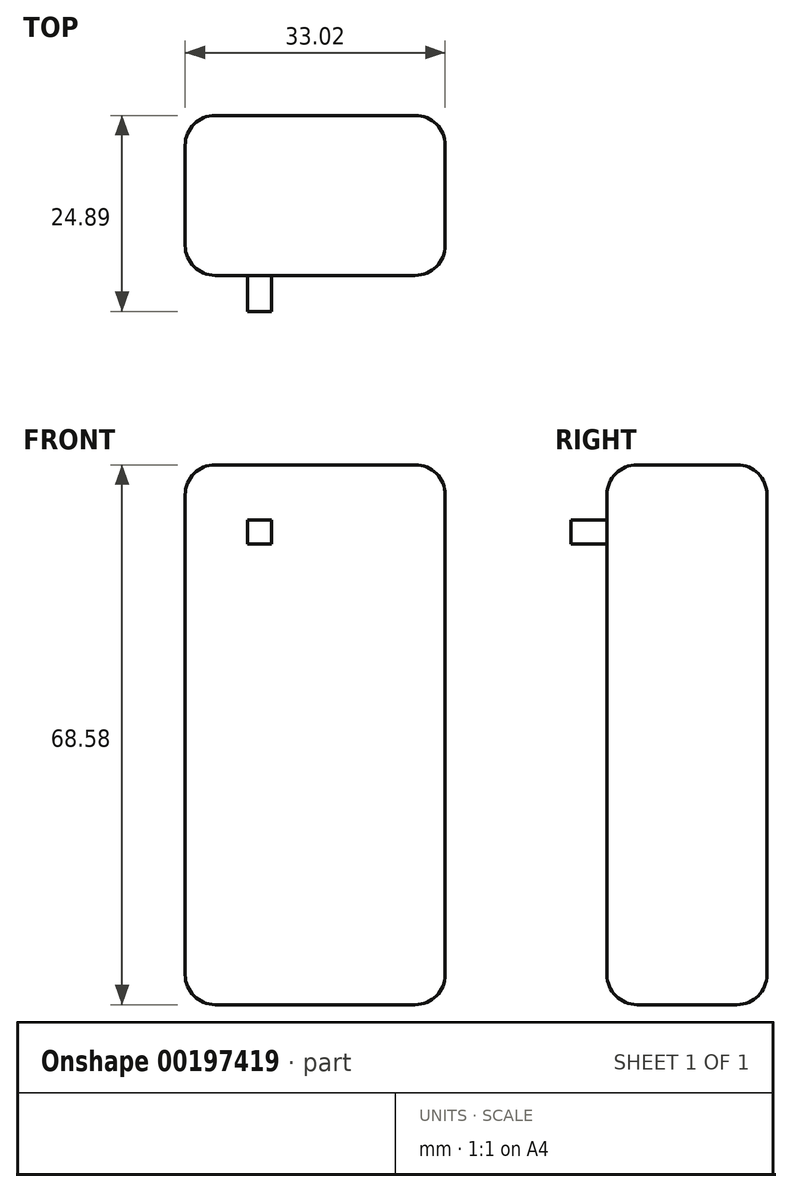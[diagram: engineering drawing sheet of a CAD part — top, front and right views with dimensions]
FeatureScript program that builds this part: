
annotation { "Feature Type Name" : "Feature", "Feature Type Description" : "" }
export const myFeature = defineFeature(function(context is Context, id is Id, definition is map)
    precondition{}
    {
        {
            var Q0;
            Q0=qCreatedBy(makeId("Front.planeOp"),FACE);
            var sketch = newSketch(context, id + "F0", { "sketchPlane" : qUnion([Q0])});
            skLineSegment(sketch, "E0.bottom", {"start": v(0, 0) * mm, "end": v(33.02, 0) * mm});
            skLineSegment(sketch, "E0.top", {"start": v(0, 68.58) * mm, "end": v(33.02, 68.58) * mm});
            skLineSegment(sketch, "E0.left", {"start": v(0, 0) * mm, "end": v(0, 68.58) * mm});
            skLineSegment(sketch, "E0.right", {"start": v(33.02, 0) * mm, "end": v(33.02, 68.58) * mm});
            skSolve(sketch);
        }
        {
            var Q0;
            Q0 = qSketchRegion(id + "F0", true);
            extrude(context, id + "F1", {"entities" : qUnion([Q0]), "depth" : 20.32 * mm});
        }
        {
            var Q0;
            Q0=makeQuery(id+"F1.opExtrude","CAP_EDGE",EDGE,{"disambiguationData":[OSD([sQuery(id+"F0.wireOp",EDGE,"E0.right")])],"isStart":false});
            var Q1;
            Q1=makeQuery(id+"F1.opExtrude","SWEPT_EDGE",EDGE,{"disambiguationData":[OSD([sQuery(id+"F0.wireOp",EDGE,"E0.top"),sQuery(id+"F0.wireOp",EDGE,"E0.right")])]});
            var Q2;
            Q2=makeQuery(id+"F1.opExtrude","CAP_EDGE",EDGE,{"disambiguationData":[OSD([sQuery(id+"F0.wireOp",EDGE,"E0.top")])],"isStart":false});
            var Q3;
            Q3=makeQuery(id+"F1.opExtrude","CAP_EDGE",EDGE,{"disambiguationData":[OSD([sQuery(id+"F0.wireOp",EDGE,"E0.left")])],"isStart":false});
            var Q4;
            Q4=makeQuery(id+"F1.opExtrude","CAP_EDGE",EDGE,{"disambiguationData":[OSD([sQuery(id+"F0.wireOp",EDGE,"E0.bottom")])],"isStart":false});
            var Q5;
            Q5=makeQuery(id+"F1.opExtrude","SWEPT_EDGE",EDGE,{"disambiguationData":[OSD([sQuery(id+"F0.wireOp",EDGE,"E0.bottom"),sQuery(id+"F0.wireOp",EDGE,"E0.right")])]});
            var Q6;
            Q6=makeQuery(id+"F1.opExtrude","CAP_EDGE",EDGE,{"disambiguationData":[OSD([sQuery(id+"F0.wireOp",EDGE,"E0.right")])],"isStart":true});
            var Q7;
            Q7=makeQuery(id+"F1.opExtrude","CAP_EDGE",EDGE,{"disambiguationData":[OSD([sQuery(id+"F0.wireOp",EDGE,"E0.bottom")])],"isStart":true});
            var Q8;
            Q8=makeQuery(id+"F1.opExtrude","CAP_EDGE",EDGE,{"disambiguationData":[OSD([sQuery(id+"F0.wireOp",EDGE,"E0.left")])],"isStart":true});
            var Q9;
            Q9=makeQuery(id+"F1.opExtrude","SWEPT_FACE",FACE,{"disambiguationData":[OSD([sQuery(id+"F0.wireOp",EDGE,"E0.left")])]});
            var Q10;
            Q10=makeQuery(id+"F1.opExtrude","SWEPT_FACE",FACE,{"disambiguationData":[OSD([sQuery(id+"F0.wireOp",EDGE,"E0.top")])]});
            fillet(context, id + "F2", {"entities" : qUnion([Q0, Q1, Q2, Q3, Q4, Q5, Q6, Q7, Q8, Q9, Q10]), "radius" : 3.8 * mm, "tangentPropagation" : true, "allowEdgeOverflow" : false});
        }
        {
            var Q0;
            Q0=makeQuery(id+"F1.opExtrude","CAP_FACE",FACE,{"disambiguationData":[OSD([sQuery(id+"F0.wireOp",EDGE,"E0.bottom"),sQuery(id+"F0.wireOp",EDGE,"E0.top"),sQuery(id+"F0.wireOp",EDGE,"E0.left"),sQuery(id+"F0.wireOp",EDGE,"E0.right")])],"isStart":false});
            var sketch = newSketch(context, id + "F3", { "sketchPlane" : qUnion([Q0])});
            skLineSegment(sketch, "E1.bottom", {"start": v(7.9, 61.57) * mm, "end": v(10.98, 61.57) * mm});
            skLineSegment(sketch, "E1.top", {"start": v(7.9, 58.5) * mm, "end": v(10.98, 58.5) * mm});
            skLineSegment(sketch, "E1.left", {"start": v(7.9, 61.57) * mm, "end": v(7.9, 58.5) * mm});
            skLineSegment(sketch, "E1.right", {"start": v(10.98, 61.57) * mm, "end": v(10.98, 58.5) * mm});
            skSolve(sketch);
        }
        {
            var Q0;
            Q0 = qSketchRegion(id + "F3", true);
            extrude(context, id + "F4", {"entities" : qUnion([Q0]), "operationType" : NewBodyOperationType.ADD, "depth" : 4.57 * mm});
        }
    });
